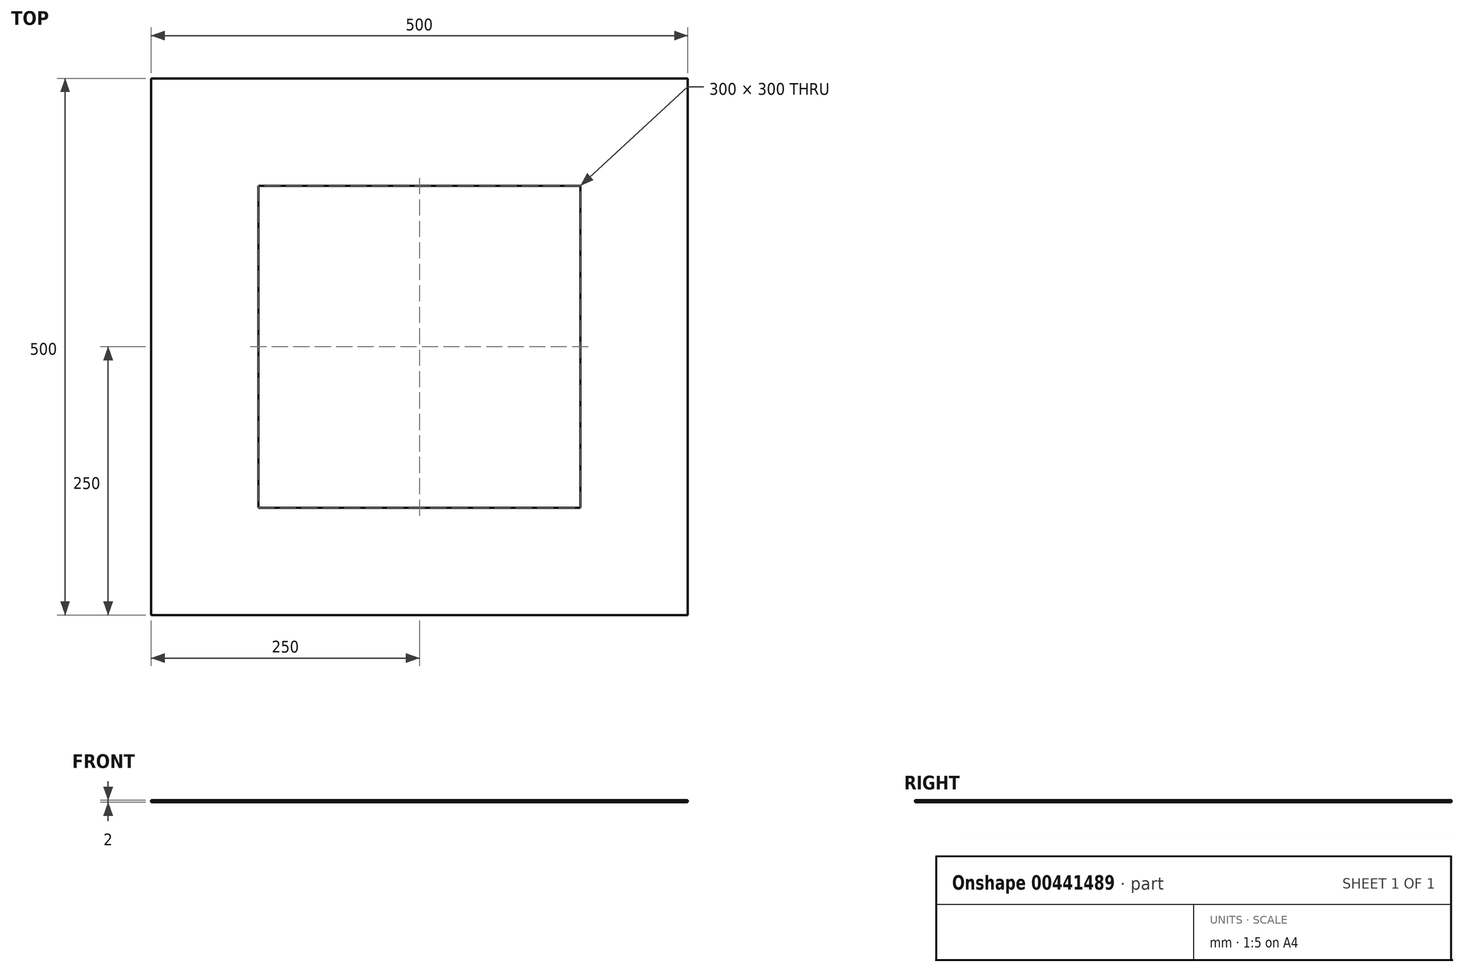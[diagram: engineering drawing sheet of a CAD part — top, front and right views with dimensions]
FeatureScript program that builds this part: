
annotation { "Feature Type Name" : "Feature", "Feature Type Description" : "" }
export const myFeature = defineFeature(function(context is Context, id is Id, definition is map)
    precondition{}
    {
        {
            var Q0;
            Q0=qCreatedBy(makeId("Top.planeOp"),FACE);
            var sketch = newSketch(context, id + "F0", { "sketchPlane" : qUnion([Q0])});
            skLineSegment(sketch, "E0.bottom", {"start": v(-250, 250) * mm, "end": v(250, 250) * mm});
            skLineSegment(sketch, "E0.top", {"start": v(-250, -250) * mm, "end": v(250, -250) * mm});
            skLineSegment(sketch, "E0.left", {"start": v(-250, 250) * mm, "end": v(-250, -250) * mm});
            skLineSegment(sketch, "E0.right", {"start": v(250, 250) * mm, "end": v(250, -250) * mm});
            skPoint(sketch, "E0.middle", {"position": v(0, 0) * mm});
            skLineSegment(sketch, "E1.bottom", {"start": v(-150, 150) * mm, "end": v(150, 150) * mm});
            skLineSegment(sketch, "E1.top", {"start": v(-150, -150) * mm, "end": v(150, -150) * mm});
            skLineSegment(sketch, "E1.left", {"start": v(-150, 150) * mm, "end": v(-150, -150) * mm});
            skLineSegment(sketch, "E1.right", {"start": v(150, 150) * mm, "end": v(150, -150) * mm});
            skSolve(sketch);
        }
        {
            var Q0;
            Q0=makeQuery(id+"F0.imprint","IMPRINT",FACE,{"disambiguationData":[TD([[makeQuery(id+"F0.imprint","IMPRINT",EDGE,{"derivedFrom":sQuery(id+"F0.wireOp",EDGE,"E0.bottom")}),-1.0]])]});
            extrude(context, id + "F1", {"entities" : qUnion([Q0]), "depth" : 2 * mm});
        }
    });
